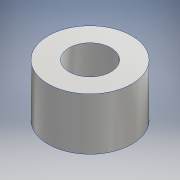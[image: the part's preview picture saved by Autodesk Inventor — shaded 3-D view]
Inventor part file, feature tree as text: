
AUTODESK INVENTOR PART (.ipt)
format: ipt  version: 2016 (Build 200138000, 138)  size: 95,744 bytes
history: native  units: mm
features: other x1, extrude x1, sketch x1
ambient origin geometry x8: Origin, YZ Plane, XZ Plane, XY Plane, X Axis, Y Axis, Z Axis, Center Point
bodies: Body1 (feature_tree)
feature tree (3):
  other  "ソリッド1"
  extrude  "押し出し1"  Depth=4.0mm
  sketch  "スケッチ1"
